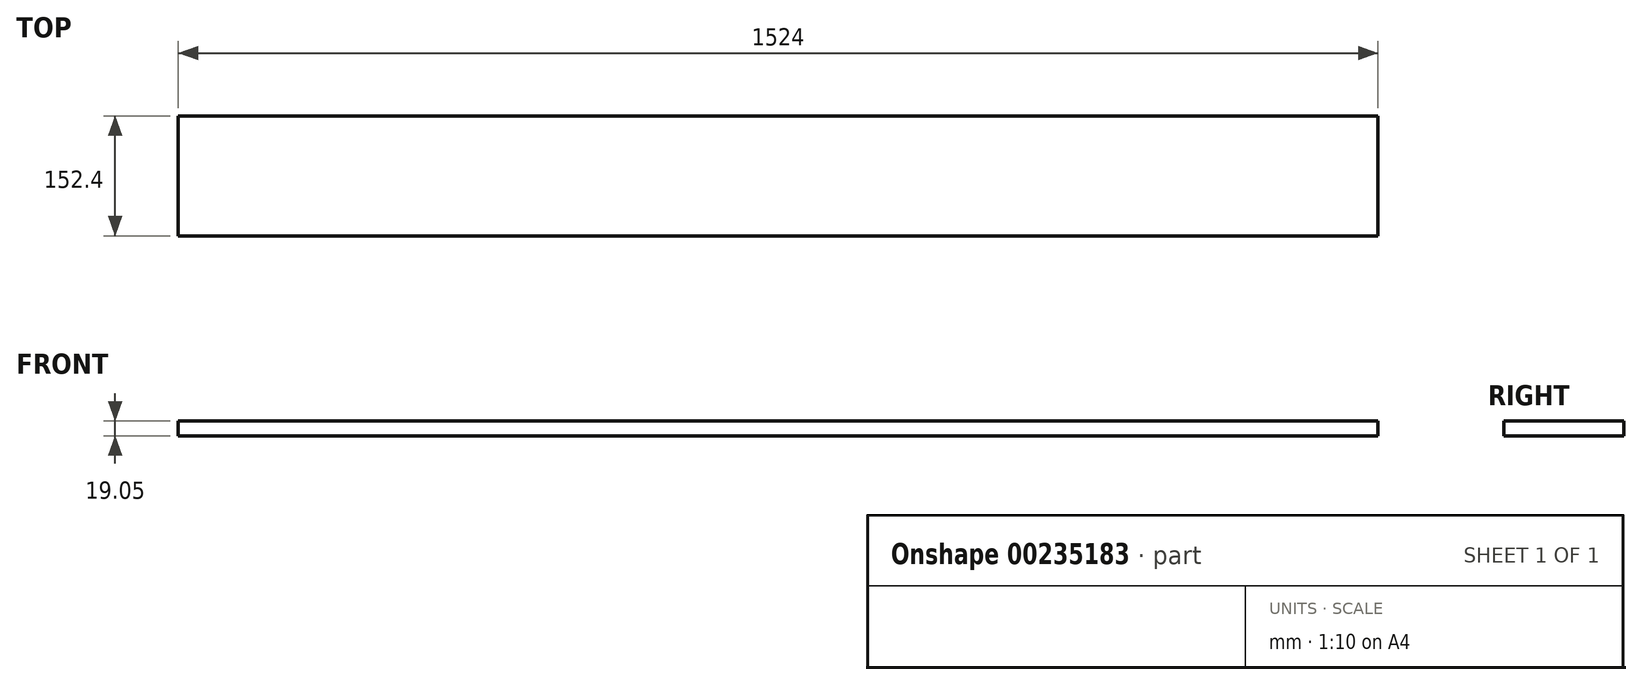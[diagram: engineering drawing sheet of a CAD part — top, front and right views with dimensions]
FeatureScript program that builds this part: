
annotation { "Feature Type Name" : "Feature", "Feature Type Description" : "" }
export const myFeature = defineFeature(function(context is Context, id is Id, definition is map)
    precondition{}
    {
        {
            var Q0;
            Q0=qCreatedBy(makeId("Top.planeOp"),FACE);
            var sketch = newSketch(context, id + "F0", { "sketchPlane" : qUnion([Q0])});
            skLineSegment(sketch, "E0.bottom", {"start": v(-762, 76.2) * mm, "end": v(762, 76.2) * mm});
            skLineSegment(sketch, "E0.top", {"start": v(-762, -76.2) * mm, "end": v(762, -76.2) * mm});
            skLineSegment(sketch, "E0.left", {"start": v(-762, 76.2) * mm, "end": v(-762, -76.2) * mm});
            skLineSegment(sketch, "E0.right", {"start": v(762, 76.2) * mm, "end": v(762, -76.2) * mm});
            skLineSegment(sketch, "E1", {"start": v(0, 0) * mm, "end": v(0, 57.63) * mm, "construction": true});
            skLineSegment(sketch, "E2", {"start": v(0, 0) * mm, "end": v(51.59, 0) * mm, "construction": true});
            skSolve(sketch);
        }
        {
            var Q0;
            Q0=makeQuery(id+"F0.imprint","IMPRINT",FACE,{"disambiguationData":[TD([[makeQuery(id+"F0.imprint","IMPRINT",EDGE,{"derivedFrom":sQuery(id+"F0.wireOp",EDGE,"E0.bottom")}),-1.0]])]});
            extrude(context, id + "F1", {"entities" : qUnion([Q0]), "depth" : 19.05 * mm});
        }
    });
